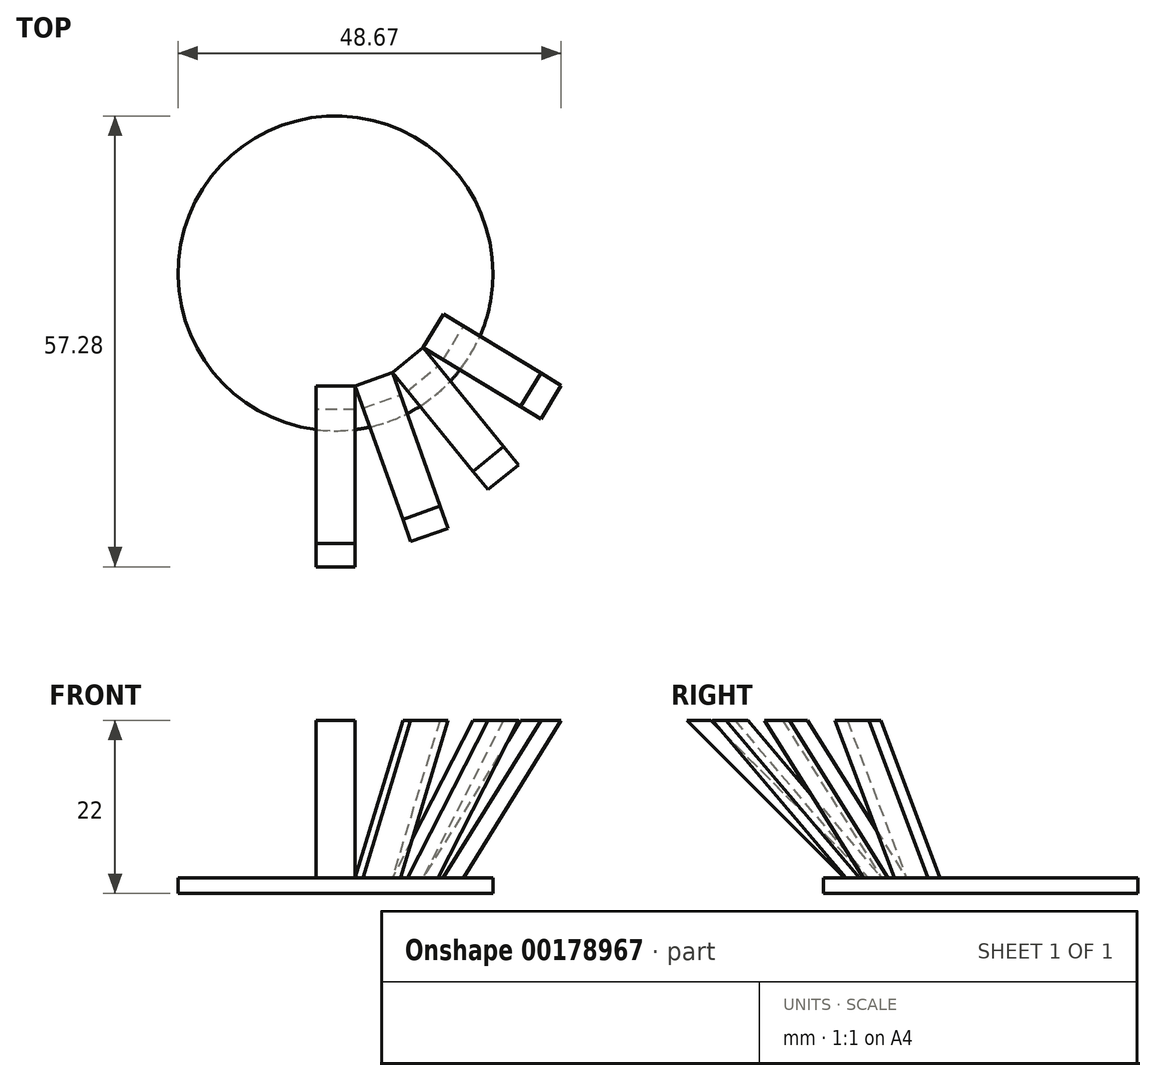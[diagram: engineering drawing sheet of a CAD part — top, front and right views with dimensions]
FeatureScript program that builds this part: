
annotation { "Feature Type Name" : "Feature", "Feature Type Description" : "" }
export const myFeature = defineFeature(function(context is Context, id is Id, definition is map)
    precondition{}
    {
        {
            var Q0;
            Q0=qCreatedBy(makeId("Right.planeOp"),FACE);
            var sketch = newSketch(context, id + "F0", { "sketchPlane" : qUnion([Q0])});
            skLineSegment(sketch, "E0", {"start": v(0, 0) * mm, "end": v(-3, 0) * mm});
            skLineSegment(sketch, "E1", {"start": v(-3, 0) * mm, "end": v(-23, 20) * mm});
            skLineSegment(sketch, "E2", {"start": v(-23, 20) * mm, "end": v(-20, 20) * mm});
            skLineSegment(sketch, "E3", {"start": v(-20, 20) * mm, "end": v(0, 0) * mm});
            skPoint(sketch, "E4", {"position": v(14.5, 0) * mm});
            skLineSegment(sketch, "E5", {"start": v(14.5, 0) * mm, "end": v(14.5, 20) * mm, "construction": true});
            skSolve(sketch);
        }
        {
            var Q0;
            Q0=qCreatedBy(makeId("Right.planeOp"),FACE);
            var Q1;
            Q1=sQuery(id+"F0.wireOp",EDGE,"E5");
            cPlane(context, id + "F1", {"entities" : qUnion([Q0, Q1]), "cplaneType" : CPlaneType.LINE_ANGLE, "offset" : 25 * mm, "angle" : 19.6 * degree, "width" : 150 * mm, "height" : 150 * mm});
        }
        {
            var Q0;
            Q0=qCreatedBy(id+"F1.planeOp",FACE);
            var sketch = newSketch(context, id + "F2", { "sketchPlane" : qUnion([Q0])});
            skLineSegment(sketch, "E6", {"start": v(0.84, 0) * mm, "end": v(3.84, 0) * mm});
            skLineSegment(sketch, "E7", {"start": v(3.84, 0) * mm, "end": v(21.84, 20) * mm});
            skLineSegment(sketch, "E8", {"start": v(21.84, 20) * mm, "end": v(18.84, 20) * mm});
            skLineSegment(sketch, "E9", {"start": v(18.84, 20) * mm, "end": v(0.84, 0) * mm});
            skLineSegment(sketch, "E10", {"start": v(0.84, 0) * mm, "end": v(0.84, 15.63) * mm, "construction": true});
            skSolve(sketch);
        }
        {
            var Q0;
            Q0=makeQuery(id+"F0.imprint","IMPRINT",FACE,{"disambiguationData":[TD([[makeQuery(id+"F0.imprint","IMPRINT",EDGE,{"derivedFrom":sQuery(id+"F0.wireOp",EDGE,"E0")}),-1.0]])]});
            extrude(context, id + "F3", {"entities" : qUnion([Q0]), "endBound" : BoundingType.SYMMETRIC, "depth" : 5 * mm});
        }
        {
            var Q0;
            Q0=qCreatedBy(makeId("Top.planeOp"),FACE);
            var sketch = newSketch(context, id + "F4", { "sketchPlane" : qUnion([Q0])});
            skCircle(sketch, "E11", {"center": v(0, 14.28) * mm, "radius": 20 * mm});
            skCircle(sketch, "E12", {"center": v(0, 14.28) * mm, "radius": 14.5 * mm, "construction": true});
            skSolve(sketch);
        }
        {
            var Q0;
            Q0=makeQuery(id+"F4.imprint","IMPRINT",FACE,{"disambiguationData":[TD([[makeQuery(id+"F4.imprint","IMPRINT",EDGE,{"derivedFrom":sQuery(id+"F4.wireOp",EDGE,"E11")}),1.0]])]});
            extrude(context, id + "F5", {"entities" : qUnion([Q0]), "oppositeDirection" : true, "depth" : 2 * mm});
        }
        {
            var Q0;
            Q0=makeQuery(id+"F2.imprint","IMPRINT",FACE,{"disambiguationData":[TD([[makeQuery(id+"F2.imprint","IMPRINT",EDGE,{"derivedFrom":sQuery(id+"F2.wireOp",EDGE,"E6")}),1.0]])]});
            extrude(context, id + "F6", {"entities" : qUnion([Q0]), "operationType" : NewBodyOperationType.ADD, "endBound" : BoundingType.SYMMETRIC, "depth" : 5 * mm});
        }
        {
            var Q0;
            Q0=sQuery(id+"F0.wireOp",EDGE,"E5");
            var Q1;
            Q1=qCreatedBy(makeId("Right.planeOp"),FACE);
            cPlane(context, id + "F7", {"entities" : qUnion([Q0, Q1]), "cplaneType" : CPlaneType.LINE_ANGLE, "offset" : 25 * mm, "angle" : 39.2 * degree, "width" : 150 * mm, "height" : 150 * mm});
        }
        {
            var Q0;
            Q0=qCreatedBy(id+"F7.planeOp",FACE);
            var sketch = newSketch(context, id + "F8", { "sketchPlane" : qUnion([Q0])});
            skLineSegment(sketch, "E13", {"start": v(3.26, 0) * mm, "end": v(6.26, 0) * mm});
            skLineSegment(sketch, "E14", {"start": v(6.26, 0) * mm, "end": v(22.46, 20) * mm});
            skLineSegment(sketch, "E15", {"start": v(22.46, 20) * mm, "end": v(19.46, 20) * mm});
            skLineSegment(sketch, "E16", {"start": v(19.46, 20) * mm, "end": v(3.26, 0) * mm});
            skLineSegment(sketch, "E17", {"start": v(3.26, 0) * mm, "end": v(3.26, 15.63) * mm, "construction": true});
            skLineSegment(sketch, "E18", {"start": v(6.26, 0) * mm, "end": v(13.71, 0) * mm, "construction": true});
            skSolve(sketch);
        }
        {
            var Q0;
            Q0=makeQuery(id+"F8.imprint","IMPRINT",FACE,{"disambiguationData":[TD([[makeQuery(id+"F8.imprint","IMPRINT",EDGE,{"derivedFrom":sQuery(id+"F8.wireOp",EDGE,"E13")}),1.0]])]});
            extrude(context, id + "F9", {"entities" : qUnion([Q0]), "operationType" : NewBodyOperationType.ADD, "endBound" : BoundingType.SYMMETRIC, "depth" : 5 * mm});
        }
        {
            var Q0;
            Q0=sQuery(id+"F0.wireOp",EDGE,"E5");
            var Q1;
            Q1=qCreatedBy(makeId("Right.planeOp"),FACE);
            cPlane(context, id + "F10", {"entities" : qUnion([Q0, Q1]), "cplaneType" : CPlaneType.LINE_ANGLE, "offset" : 25 * mm, "angle" : 58.8 * degree, "width" : 150 * mm, "height" : 150 * mm});
        }
        {
            var Q0;
            Q0=qCreatedBy(id+"F10.planeOp",FACE);
            var sketch = newSketch(context, id + "F11", { "sketchPlane" : qUnion([Q0])});
            skLineSegment(sketch, "E19", {"start": v(6.99, 0) * mm, "end": v(9.99, 0) * mm});
            skLineSegment(sketch, "E20", {"start": v(9.99, 0) * mm, "end": v(24.49, 20) * mm});
            skLineSegment(sketch, "E21", {"start": v(24.49, 20) * mm, "end": v(21.49, 20) * mm});
            skLineSegment(sketch, "E22", {"start": v(21.49, 20) * mm, "end": v(6.99, 0) * mm});
            skLineSegment(sketch, "E23", {"start": v(6.99, 0) * mm, "end": v(6.99, 15.63) * mm, "construction": true});
            skLineSegment(sketch, "E24", {"start": v(9.99, 0) * mm, "end": v(15.74, 0) * mm, "construction": true});
            skSolve(sketch);
        }
        {
            var Q0;
            Q0=makeQuery(id+"F11.imprint","IMPRINT",FACE,{"disambiguationData":[TD([[makeQuery(id+"F11.imprint","IMPRINT",EDGE,{"derivedFrom":sQuery(id+"F11.wireOp",EDGE,"E19")}),1.0]])]});
            extrude(context, id + "F12", {"entities" : qUnion([Q0]), "operationType" : NewBodyOperationType.ADD, "endBound" : BoundingType.SYMMETRIC, "depth" : 5 * mm});
        }
    });
